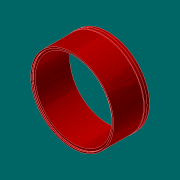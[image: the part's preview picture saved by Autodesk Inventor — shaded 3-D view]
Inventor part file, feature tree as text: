
AUTODESK INVENTOR PART (.ipt)
format: ipt  version: 2017.3 (Build 213257000, 257)  size: 145,408 bytes
history: native  units: in
note: dims shown in document units (in); Inventor stores cm internally (conversion verified against a paired STEP export)
features: extrude x4, sketch x4, chamfer x2, fillet x1
ambient origin geometry x8: Origin, YZ Plane, XZ Plane, XY Plane, X Axis, Y Axis, Z Axis, Center Point
bodies: Solid1 (feature_tree)
feature tree (11):
  extrude  "Extrusion1"  Depth=31.0in
  extrude  "Extrusion2"  Depth=12.8346in
  extrude  "Extrusion3"  Depth=1.0in
  chamfer  "Chamfer1"  Distance=1.0in
  extrude  "Extrusion4"  Depth=0.0312in TaperAngle=45.0deg
  fillet  "Fillet1"  Radius=30.0in
  chamfer  "Chamfer2"  Distance=0.5in
  sketch  "Sketch1"  dims[d0=28.5in d1=31.0in]
  sketch  "Sketch2"  dims[d2=12.8346in d3=0.0in d4=31.25in]
  sketch  "Sketch3"  dims[d5=2.0in d6=0.0in d7=30.98in d8=1.0in d9=0.0in]
  sketch  "Sketch4"  dims[d10=0.125in d11=0.125in d12=45.0deg d13=30.0in d14=0.5in d15=0.0in d16=0.0312in d17=0.0312in d18=0.125in d19=45.0deg]
